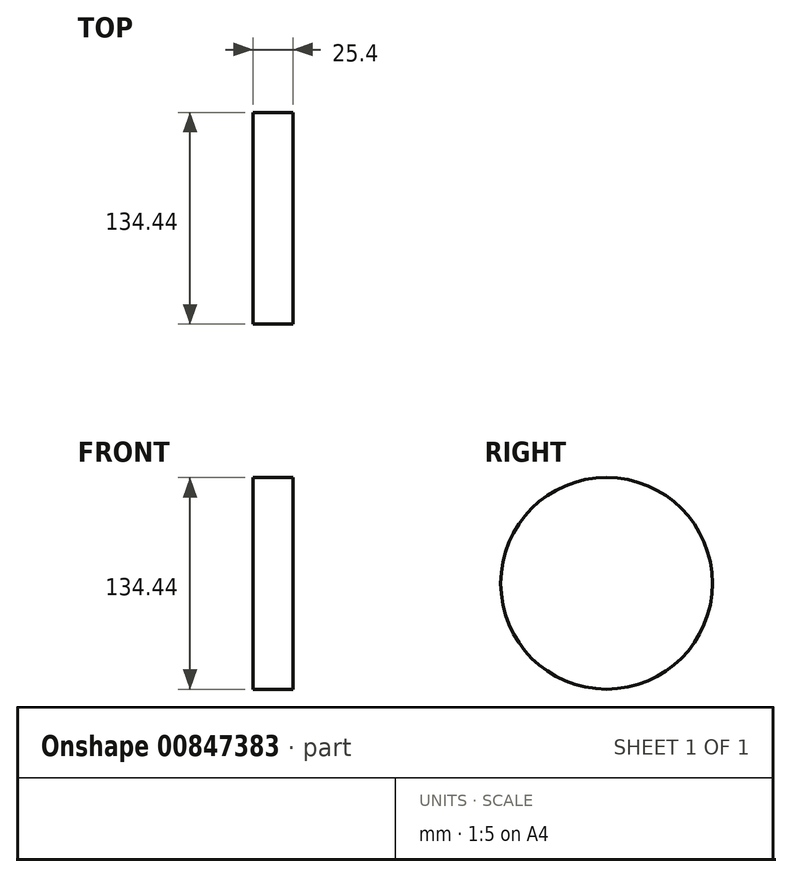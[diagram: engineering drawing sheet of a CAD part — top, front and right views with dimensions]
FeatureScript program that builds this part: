
annotation { "Feature Type Name" : "Feature", "Feature Type Description" : "" }
export const myFeature = defineFeature(function(context is Context, id is Id, definition is map)
    precondition{}
    {
        {
            var Q0;
            Q0=qCreatedBy(makeId("Right.planeOp"),FACE);
            var sketch = newSketch(context, id + "F0", { "sketchPlane" : qUnion([Q0])});
            skCircle(sketch, "E0", {"center": v(0, 0) * mm, "radius": 67.22 * mm});
            skCircle(sketch, "E1", {"center": v(-80.2, 79.2) * mm, "radius": 25.32 * mm});
            skCircle(sketch, "E2", {"center": v(-60.48, 79.26) * mm, "radius": 14.25 * mm});
            skSolve(sketch);
        }
        {
            var Q0;
            Q0=makeQuery(id+"F0.imprint","IMPRINT",FACE,{"disambiguationData":[TD([[makeQuery(id+"F0.imprint","IMPRINT",EDGE,{"derivedFrom":sQuery(id+"F0.wireOp",EDGE,"E0")}),1.0]])]});
            extrude(context, id + "F1", {"entities" : qUnion([Q0]), "depth" : 25.4 * mm, "offsetDistance" : 25.4 * mm});
        }
    });
